# Revit family: HVAC_Other_Enertech_CTC_EL-42
name_source: partatom
category: Specialty Equipment
revit_build: Autodesk Revit 2018 (Build: 20170223_1515(x64)
units: mm (PartAtom-declared; Revit-internal decimal feet)

## family parameters
Always vertical = No
Cut with Voids When Loaded = No
OmniClass Number = 23.75.00.00
OmniClass Title = Climate Control (HVAC)
Part Type = Normal
Room Calculation Point = No
Round Connector Dimension = Use Diameter
Shared = No
Work Plane-Based = No

## types (1)
- CTC EL 42 400V3N
    AssetType = Fixed
    BIMObjectName = HVAC_Other_Enertech_CTC_EL-42
    Brand = CTC
    Category = electrical heating
    Color = white
    Cost = 0 $
    Description = A compact and easy-to-install electric flow heater with seven power stages: from 6 kW to 42 kW. Often used as additional heat in heat pump systems
    DurationUnit = Year
    EANNumber = 7333077098360
    ElectricalDeviceNominalPower = 42000 W
    EnergyClass_HotWater_TapProfile = A/XL
    GroupFuse = 63 A
    HasProtectiveEarth = Yes
    IP_Code = IP21
    IfcExportAs = IfcElectricalDeviceCommon
    IfcExportType = HEATER
    Manufacturer = Enertech AB
    ManufacturerCountry = Sweden
    ManufacturerName = Enertech AB
    ManufacturerURL = https://ctc.se
    Material = Steel
    MaxOperatingPressureThermalStore = 7 bar
    Model = CTC EL 42
    ModelNumber = 589843001
    NBSDescription = Air to water heat pumps
    NBSReference = 90-40-40/320
    Name = CTC_EL-42
    NominalCurrent = 0 A
    NominalDepth = 402 mm
    NominalFrequencyRange = 50 Hz
    NominalHeight = 712 mm
    NominalVoltage = 400 V
    NominalWidth = 354 mm
    OutputRangeIimmersionHeater = 6-42 kW
    PhaseAngle = 0.00°
    PowerFactor = 0 W
    ProductInformation = A compact and easy-to-install electric flow heater with seven power stages: from 6 kW to 42 kW. Often used as additional heat in heat pump systems
    PumpMainMaterial = Stainless Steel
    PumpSecondaryMaterial = Brass
    RatedCurrent = 61 A
    RatedVoltage = 1200 V
    Shape = Rectangular
    Size = 402x354x712 mm
    SoundPowerLWA = 35 dB(A)
    Touchscreen = No
    UNSPSCCode = 40102003
    URL = https://ctc-heating.com
    Uniclass2 = Pr_40_70_65
    Uniclass2015Description = Preparation catering equipment
    Uniclass2015Reference = Pr_40_70_65
    UsageCurrent = 0 A
    Version = 1
    VersionDate = 24/05/2022
    WarrantyDurationUnit = Year
    WaterVolumeHeathingSystem = 10 liters
    Weight = 33 kg

## geometry (parser evidence)
native form markers: Sweep x4
no freeform markers — native parametric forms only
